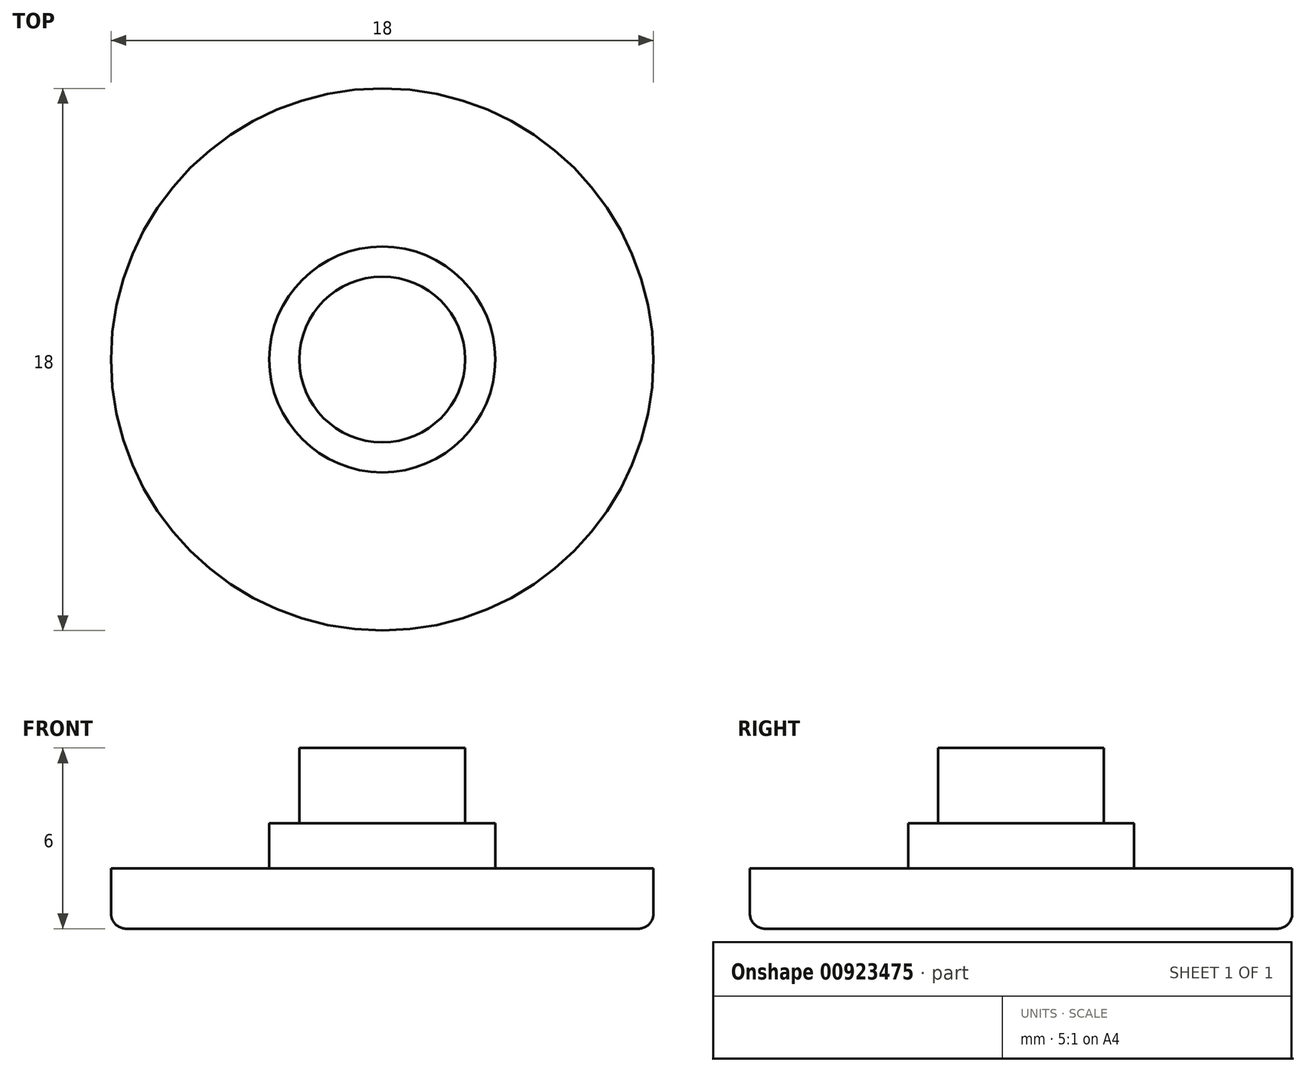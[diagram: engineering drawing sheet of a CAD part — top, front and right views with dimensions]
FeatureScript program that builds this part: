
annotation { "Feature Type Name" : "Feature", "Feature Type Description" : "" }
export const myFeature = defineFeature(function(context is Context, id is Id, definition is map)
    precondition{}
    {
        {
            var Q0;
            Q0=qCreatedBy(makeId("Front.planeOp"),FACE);
            var sketch = newSketch(context, id + "F0", { "sketchPlane" : qUnion([Q0])});
            skLineSegment(sketch, "E0", {"start": v(0, 4) * mm, "end": v(-2.75, 4) * mm});
            skLineSegment(sketch, "E1", {"start": v(-2.75, 4) * mm, "end": v(-2.75, 1.5) * mm});
            skLineSegment(sketch, "E2", {"start": v(-3.75, 0) * mm, "end": v(-9, 0) * mm});
            skLineSegment(sketch, "E3", {"start": v(-9, 0) * mm, "end": v(-9, -1.5) * mm});
            skLineSegment(sketch, "E4", {"start": v(-8.5, -2) * mm, "end": v(0, -2) * mm});
            skLineSegment(sketch, "E5", {"start": v(0, -2) * mm, "end": v(0, 4) * mm});
            skLineSegment(sketch, "E6", {"start": v(-3.75, 0) * mm, "end": v(-3.75, 1.5) * mm});
            skLineSegment(sketch, "E7", {"start": v(-3.75, 1.5) * mm, "end": v(-2.75, 1.5) * mm});
            skPoint(sketch, "E8.orphan", {"position": v(-2.75, 0) * mm});
            skPoint(sketch, "E9.visualSharp", {"position": v(-9, -2) * mm});
            skArc(sketch, "E9.filletArc", {"start": v(-9, -1.5) * mm, "mid": v(-8.85, -1.85) * mm, "end": v(-8.5, -2) * mm});
            skSolve(sketch);
        }
        {
            var Q0;
            Q0 = qSketchRegion(id + "F0", true);
            var Q1;
            Q1=sQuery(id+"F0.wireOp",EDGE,"E5");
            revolve(context, id + "F1", {"surfaceOperationType" : NewSurfaceOperationType.NEW, "entities" : qUnion([Q0]), "axis" : qUnion([Q1]), "revolveType" : RevolveType.FULL});
        }
    });
